# Revit family: Atdec-Ceiling_Dislpay_Mount-TH-3070-CT-
name_source: partatom
category: Generic Models
revit_build: Autodesk Revit 2016 (Build: 20150220_1215(x64)
units: mm (PartAtom-declared; Revit-internal decimal feet)

## family parameters
Can host rebar = No
Cut with Voids When Loaded = No
Host = Face
Part Type = Normal
Room Calculation Point = No
Round Connector Dimension = Use Diameter
Shared = No

## types (2) — shared parameters
Assembly Code = E1010800
Colour Options = Black
Default Elevation = 1219 mm
Flat screen maximum supported weight = 65kg (143lb)
Manufacturer = Atdec
Master Carton Dimensions = -
Material = Steel and Aluminum
Maximum distance from wall (mm) = -
Minimum distance from wall (mm) = -
Pan adjustment = Fixed or 360° around pole
Pole Finish = ATD-Powdercoat Black
Product Family = Wall Mount Rail
Product Information Link = https://www.atdec.com.au
Range of Motion = Tilt
Security features = -
Single units per master pack = 1
Tilt adjustment = 20° of downward tilt
URL = www.atdec.com.au
Universal Height (mm) = From 200 to 500
Universal Width (mm) = From 200 to 800
VESA mounting hole pattern, mm = 200x200, 200x300, 200x400, 300x200, 300x300, 400x200, 400x300, 400x400, 600x200, 600x400, 800x200, 800x400
Weight, Master Carton = -

## per-type parameters (varying)
| type | CTL | CTS | Description | Low Pole Length | Single Unit Dimensions | Top Pole Length | UPC Code | Warranty | Weight, Single Unit |
| TH-3070-CTL | Yes | No | Medium to large display ceiling mount, long pole | 868 mm  [stored 2.84777 ft] | 1060mm (41.7") Lenght, 300mm (11.8") Width, 150mm (5.9") Height | 1000 mm  [stored 3.28084 ft] | 881493007543 | 10 years if purchased after Jan 1, 201 | 15kg (33lb) |
| TH-3070-CTS | No | Yes | Medium to display ceiling mount, short pole | 450 mm  [stored 1.47638 ft] | 930mm (36.6") Lenght, 300mm (11.8") Width, 150mm (5.9") Height | 450 mm  [stored 1.47638 ft] | 881493007567 | 10 years | 12kg (26.4lb) |

note: column(s) folded — value = type name in every type: Model

note: [stored X ft] marks values corroborated as IEEE doubles in the binary element streams (Revit-internal decimal feet)

## geometry (parser evidence)
native form markers: Sweep x3
no freeform markers — native parametric forms only
